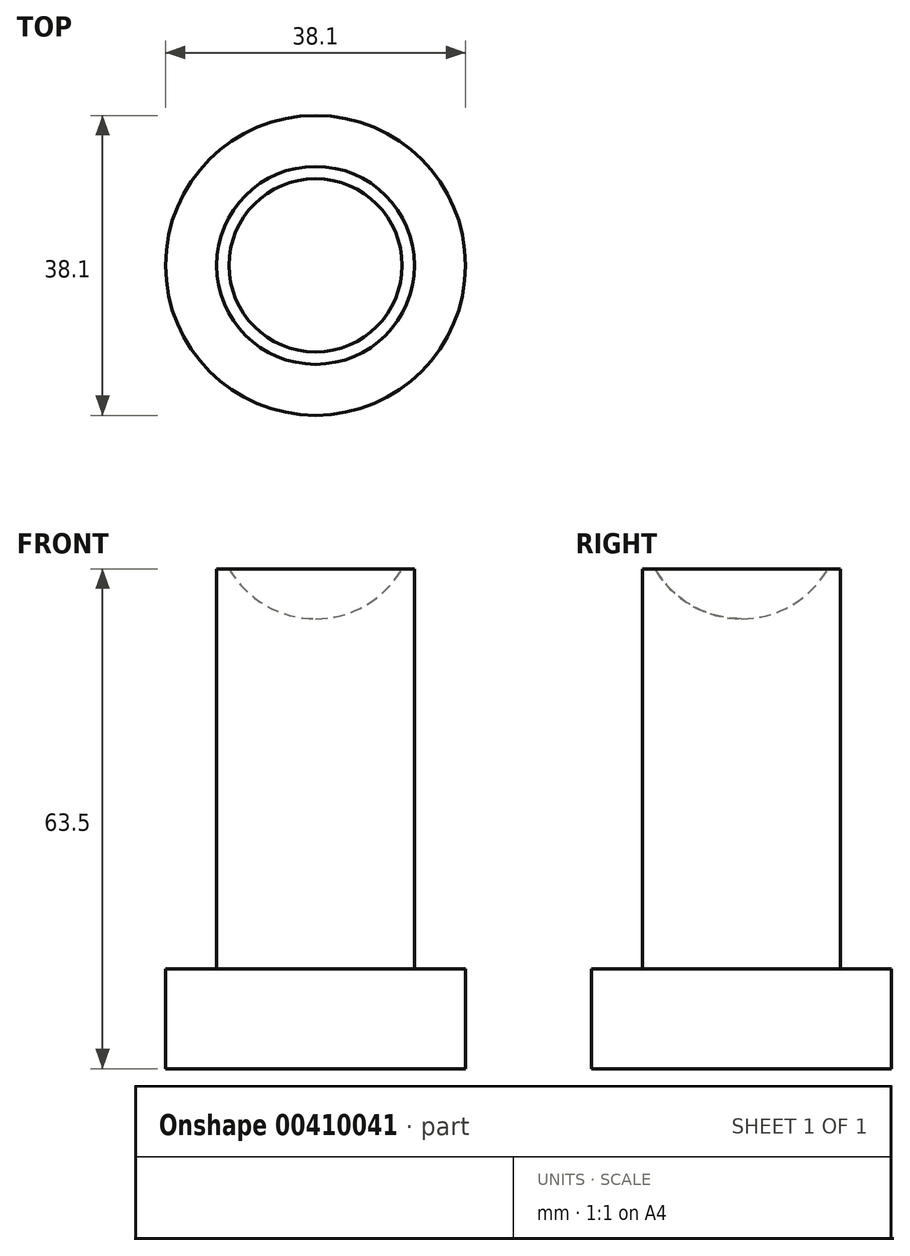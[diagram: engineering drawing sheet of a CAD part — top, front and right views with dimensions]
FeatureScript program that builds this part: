
annotation { "Feature Type Name" : "Feature", "Feature Type Description" : "" }
export const myFeature = defineFeature(function(context is Context, id is Id, definition is map)
    precondition{}
    {
        {
            var Q0;
            Q0=qCreatedBy(makeId("Top.planeOp"),FACE);
            var sketch = newSketch(context, id + "F0", { "sketchPlane" : qUnion([Q0])});
            skCircle(sketch, "E0", {"center": v(0, 0) * mm, "radius": 19.05 * mm});
            skSolve(sketch);
        }
        {
            var Q0;
            Q0 = qSketchRegion(id + "F0", true);
            extrude(context, id + "F1", {"entities" : qUnion([Q0]), "depth" : 12.7 * mm});
        }
        {
            var Q0;
            Q0=makeQuery(id+"F1.opExtrude","CAP_FACE",FACE,{"disambiguationData":[OSD([sQuery(id+"F0.wireOp",EDGE,"E0")])],"isStart":false});
            var sketch = newSketch(context, id + "F2", { "sketchPlane" : qUnion([Q0])});
            skCircle(sketch, "E1", {"center": v(0, 0) * mm, "radius": 12.57 * mm});
            skSolve(sketch);
        }
        {
            var Q0;
            Q0 = qSketchRegion(id + "F2", true);
            extrude(context, id + "F3", {"entities" : qUnion([Q0]), "operationType" : NewBodyOperationType.ADD, "depth" : 50.8 * mm});
        }
        {
            var Q0;
            Q0=qCreatedBy(makeId("Right.planeOp"),FACE);
            var sketch = newSketch(context, id + "F4", { "sketchPlane" : qUnion([Q0])});
            skArc(sketch, "E2", {"start": v(0, 57.15) * mm, "mid": v(7.05, 59.29) * mm, "end": v(11.73, 64.98) * mm});
            skLineSegment(sketch, "E3", {"start": v(0, 57.15) * mm, "end": v(0, 64.98) * mm});
            skLineSegment(sketch, "E4", {"start": v(0, 64.98) * mm, "end": v(11.73, 64.98) * mm});
            skSolve(sketch);
        }
        {
            var Q0;
            Q0=makeQuery(id+"F4.imprint","IMPRINT",FACE,{"disambiguationData":[TD([[makeQuery(id+"F4.imprint","IMPRINT",EDGE,{"derivedFrom":sQuery(id+"F4.wireOp",EDGE,"E2")}),1.0]])]});
            var Q1;
            Q1=sQuery(id+"F4.wireOp",EDGE,"E3");
            revolve(context, id + "F5", {"operationType" : NewBodyOperationType.REMOVE, "entities" : qUnion([Q0]), "axis" : qUnion([Q1]), "revolveType" : RevolveType.FULL, "oppositeDirection" : true});
        }
    });
